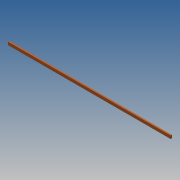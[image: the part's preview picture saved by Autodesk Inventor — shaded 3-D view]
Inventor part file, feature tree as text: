
AUTODESK INVENTOR PART (.ipt)
format: ipt  version: 2013 (Build 170138000, 138)  size: 68,096 bytes
history: native  units: in
note: dims shown in document units (in); Inventor stores cm internally (conversion verified against a paired STEP export)
features: extrude x1, sketch x1
ambient origin geometry x8: Origin, YZ Plane, XZ Plane, XY Plane, X Axis, Y Axis, Z Axis, Center Point
bodies: Solid1 (feature_tree)
feature tree (2):
  extrude  "Extrusion1"  Depth=3.5in
  sketch  "Sketch1"  dims[d0=1.5in d1=3.5in d2=192.0in d3=0.0in]
